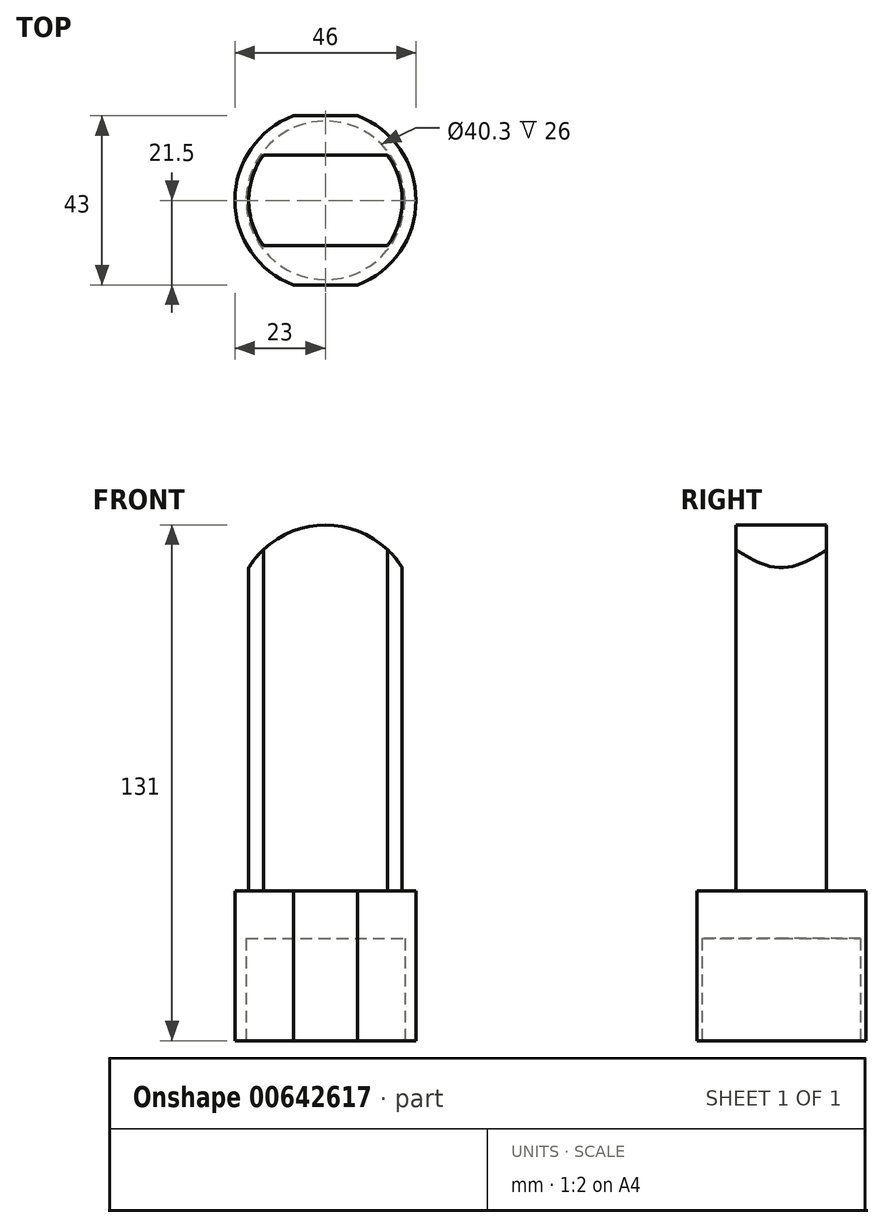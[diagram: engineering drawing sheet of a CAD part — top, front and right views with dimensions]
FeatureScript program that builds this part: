
annotation { "Feature Type Name" : "Feature", "Feature Type Description" : "" }
export const myFeature = defineFeature(function(context is Context, id is Id, definition is map)
    precondition{}
    {
        {
            var Q0;
            Q0=qCreatedBy(makeId("Top.planeOp"),FACE);
            var sketch = newSketch(context, id + "F0", { "sketchPlane" : qUnion([Q0])});
            skArc(sketch, "E0", {"start": v(-8.17, 21.5) * mm, "mid": v(-23, 0) * mm, "end": v(-8.17, -21.5) * mm});
            skLineSegment(sketch, "E1", {"start": v(-8.17, 21.5) * mm, "end": v(8.17, 21.5) * mm});
            skLineSegment(sketch, "E2.MirrorCS", {"start": v(-8.17, -21.5) * mm, "end": v(8.17, -21.5) * mm});
            skArc(sketch, "E3.trimOffspring", {"start": v(8.17, -21.5) * mm, "mid": v(23, 0) * mm, "end": v(8.17, 21.5) * mm});
            skSolve(sketch);
        }
        {
            var Q0;
            Q0=makeQuery(id+"F0.imprint","IMPRINT",FACE,{"disambiguationData":[TD([[makeQuery(id+"F0.imprint","IMPRINT",EDGE,{"derivedFrom":sQuery(id+"F0.wireOp",EDGE,"E0")}),1.0]])]});
            extrude(context, id + "F1", {"entities" : qUnion([Q0]), "depth" : 38 * mm, "offsetDistance" : 25 * mm});
        }
        {
            var Q0;
            Q0=makeQuery(id+"F1.opExtrude","CAP_FACE",FACE,{"disambiguationData":[OSD([sQuery(id+"F0.wireOp",EDGE,"E0"),sQuery(id+"F0.wireOp",EDGE,"E1"),sQuery(id+"F0.wireOp",EDGE,"E2.MirrorCS"),sQuery(id+"F0.wireOp",EDGE,"E3.trimOffspring")])],"isStart":true});
            var sketch = newSketch(context, id + "F2", { "sketchPlane" : qUnion([Q0])});
            skCircle(sketch, "E4", {"center": v(0, 0) * mm, "radius": 20.15 * mm});
            skSolve(sketch);
        }
        {
            var Q0;
            Q0=makeQuery(id+"F2.imprint","IMPRINT",FACE,{"disambiguationData":[TD([[makeQuery(id+"F2.imprint","IMPRINT",EDGE,{"derivedFrom":sQuery(id+"F2.wireOp",EDGE,"E4")}),1.0]])]});
            extrude(context, id + "F3", {"entities" : qUnion([Q0]), "operationType" : NewBodyOperationType.REMOVE, "depth" : 26 * mm, "offsetDistance" : 25 * mm});
        }
        {
            var Q0;
            Q0=makeQuery(id+"F1.opExtrude","CAP_FACE",FACE,{"disambiguationData":[OSD([sQuery(id+"F0.wireOp",EDGE,"E0"),sQuery(id+"F0.wireOp",EDGE,"E1"),sQuery(id+"F0.wireOp",EDGE,"E2.MirrorCS"),sQuery(id+"F0.wireOp",EDGE,"E3.trimOffspring")])],"isStart":false});
            var sketch = newSketch(context, id + "F4", { "sketchPlane" : qUnion([Q0])});
            skArc(sketch, "E5", {"start": v(-15.75, 11.5) * mm, "mid": v(-19.5, 0) * mm, "end": v(-15.75, -11.5) * mm});
            skLineSegment(sketch, "E6", {"start": v(-15.75, 11.5) * mm, "end": v(15.75, 11.5) * mm});
            skLineSegment(sketch, "E7.MirrorCS", {"start": v(-15.75, -11.5) * mm, "end": v(15.75, -11.5) * mm});
            skArc(sketch, "E8.trimOffspring", {"start": v(15.75, -11.5) * mm, "mid": v(19.5, 0) * mm, "end": v(15.75, 11.5) * mm});
            skSolve(sketch);
        }
        {
            var Q0;
            Q0=makeQuery(id+"F4.imprint","IMPRINT",FACE,{"disambiguationData":[TD([[makeQuery(id+"F4.imprint","IMPRINT",EDGE,{"derivedFrom":sQuery(id+"F4.wireOp",EDGE,"E5")}),1.0]])]});
            extrude(context, id + "F5", {"entities" : qUnion([Q0]), "operationType" : NewBodyOperationType.ADD, "depth" : 93 * mm, "offsetDistance" : 25 * mm});
        }
        {
            var Q0;
            Q0=makeQuery(id+"F5.opExtrude","SWEPT_FACE",FACE,{"disambiguationData":[OSD([sQuery(id+"F4.wireOp",EDGE,"E7.MirrorCS")])]});
            var sketch = newSketch(context, id + "F6", { "sketchPlane" : qUnion([Q0])});
            skCircle(sketch, "E9", {"center": v(0, 108) * mm, "radius": 23 * mm});
            skPoint(sketch, "E9.centerSnap0", {"position": v(0, 131) * mm});
            skLineSegment(sketch, "E10", {"start": v(22.75, 111.38) * mm, "end": v(46.26, 144.92) * mm});
            skLineSegment(sketch, "E11", {"start": v(46.26, 144.92) * mm, "end": v(-20.86, 152.16) * mm});
            skLineSegment(sketch, "E12", {"start": v(-20.86, 152.16) * mm, "end": v(-47.93, 122.8) * mm});
            skLineSegment(sketch, "E13", {"start": v(-47.93, 122.8) * mm, "end": v(-22.97, 109.1) * mm});
            skSolve(sketch);
        }
        {
            var Q0;
            {var subQ0=sQuery(id+"F6.wireOp",EDGE,"E10");Q0=makeQuery(id+"F6.imprint","IMPRINT",FACE,{"disambiguationData":[TD([[makeQuery(id+"F6.imprint","IMPRINT",EDGE,{"derivedFrom":subQ0}),1.0]])]});}
            var Q1;
            {var subQ0=sQuery(id+"F6.wireOp",EDGE,"E9");var subQ1=sQuery(id+"F4.wireOp",EDGE,"E7.MirrorCS");var subQ2=makeQuery(id+"F5.opExtrude","CAP_EDGE",EDGE,{"disambiguationData":[OSD([subQ1])],"isStart":false});var subQ3=makeQuery(id+"F6.imprint","INTERSECT",VERTEX,{"derivedFrom":[subQ2,subQ0]});Q1=makeQuery(id+"F6.imprint","IMPRINT",FACE,{"disambiguationData":[TD([[makeQuery(id+"F6.imprint","IMPRINT",EDGE,{"disambiguationData":[TD([[subQ3,-1.0]])],"derivedFrom":subQ0}),-1.0]])]});}
            var Q2;
            {var subQ0=sQuery(id+"F6.wireOp",EDGE,"E9");var subQ1=sQuery(id+"F4.wireOp",EDGE,"E7.MirrorCS");var subQ4=makeQuery(id+"F5.opExtrude","CAP_EDGE",EDGE,{"disambiguationData":[OSD([subQ1])],"isStart":false});var subQ5=makeQuery(id+"F6.imprint","INTERSECT",VERTEX,{"derivedFrom":[subQ4,subQ0]});Q2=makeQuery(id+"F6.imprint","IMPRINT",FACE,{"disambiguationData":[TD([[makeQuery(id+"F6.imprint","IMPRINT",EDGE,{"disambiguationData":[TD([[subQ5,1.0]])],"derivedFrom":subQ0}),-1.0]])]});}
            extrude(context, id + "F7", {"entities" : qUnion([Q0, Q1, Q2]), "operationType" : NewBodyOperationType.REMOVE, "endBound" : BoundingType.THROUGH_ALL, "depth" : 25 * mm, "offsetDistance" : 25 * mm});
        }
        {
            var Q0;
            {var subQ0=sQuery(id+"F6.wireOp",EDGE,"E10");Q0=makeQuery(id+"F6.imprint","IMPRINT",FACE,{"disambiguationData":[TD([[makeQuery(id+"F6.imprint","IMPRINT",EDGE,{"derivedFrom":subQ0}),1.0]])]});}
            var Q1;
            {var subQ0=sQuery(id+"F6.wireOp",EDGE,"E9");var subQ1=sQuery(id+"F4.wireOp",EDGE,"E7.MirrorCS");var subQ2=makeQuery(id+"F5.opExtrude","CAP_EDGE",EDGE,{"disambiguationData":[OSD([subQ1])],"isStart":false});var subQ3=makeQuery(id+"F6.imprint","INTERSECT",VERTEX,{"derivedFrom":[subQ2,subQ0]});Q1=makeQuery(id+"F6.imprint","IMPRINT",FACE,{"disambiguationData":[TD([[makeQuery(id+"F6.imprint","IMPRINT",EDGE,{"disambiguationData":[TD([[subQ3,-1.0]])],"derivedFrom":subQ0}),-1.0]])]});}
            var Q2;
            {var subQ0=sQuery(id+"F6.wireOp",EDGE,"E9");var subQ1=sQuery(id+"F4.wireOp",EDGE,"E7.MirrorCS");var subQ4=makeQuery(id+"F5.opExtrude","CAP_EDGE",EDGE,{"disambiguationData":[OSD([subQ1])],"isStart":false});var subQ5=makeQuery(id+"F6.imprint","INTERSECT",VERTEX,{"derivedFrom":[subQ4,subQ0]});Q2=makeQuery(id+"F6.imprint","IMPRINT",FACE,{"disambiguationData":[TD([[makeQuery(id+"F6.imprint","IMPRINT",EDGE,{"disambiguationData":[TD([[subQ5,1.0]])],"derivedFrom":subQ0}),-1.0]])]});}
            extrude(context, id + "F8", {"entities" : qUnion([Q0, Q1, Q2]), "operationType" : NewBodyOperationType.REMOVE, "endBound" : BoundingType.THROUGH_ALL, "oppositeDirection" : true, "depth" : 25 * mm, "offsetDistance" : 25 * mm});
        }
        {
            var Q0;
            Q0=makeQuery(id+"F1.opExtrude","CAP_FACE",FACE,{"disambiguationData":[OSD([sQuery(id+"F0.wireOp",EDGE,"E0"),sQuery(id+"F0.wireOp",EDGE,"E1"),sQuery(id+"F0.wireOp",EDGE,"E2.MirrorCS"),sQuery(id+"F0.wireOp",EDGE,"E3.trimOffspring")])],"isStart":true});
            var sketch = newSketch(context, id + "F9", { "sketchPlane" : qUnion([Q0])});
            skCircle(sketch, "E14", {"center": v(0, 0) * mm, "radius": 20.15 * mm});
            skSolve(sketch);
        }
        {
            var Q0;
            Q0=makeQuery(id+"F9.imprint","IMPRINT",FACE,{"disambiguationData":[TD([[makeQuery(id+"F9.imprint","IMPRINT",EDGE,{"derivedFrom":sQuery(id+"F9.wireOp",EDGE,"E14")}),1.0]])]});
            extrude(context, id + "F10", {"entities" : qUnion([Q0]), "operationType" : NewBodyOperationType.REMOVE, "oppositeDirection" : true, "depth" : 26 * mm, "offsetDistance" : 25 * mm});
        }
    });
